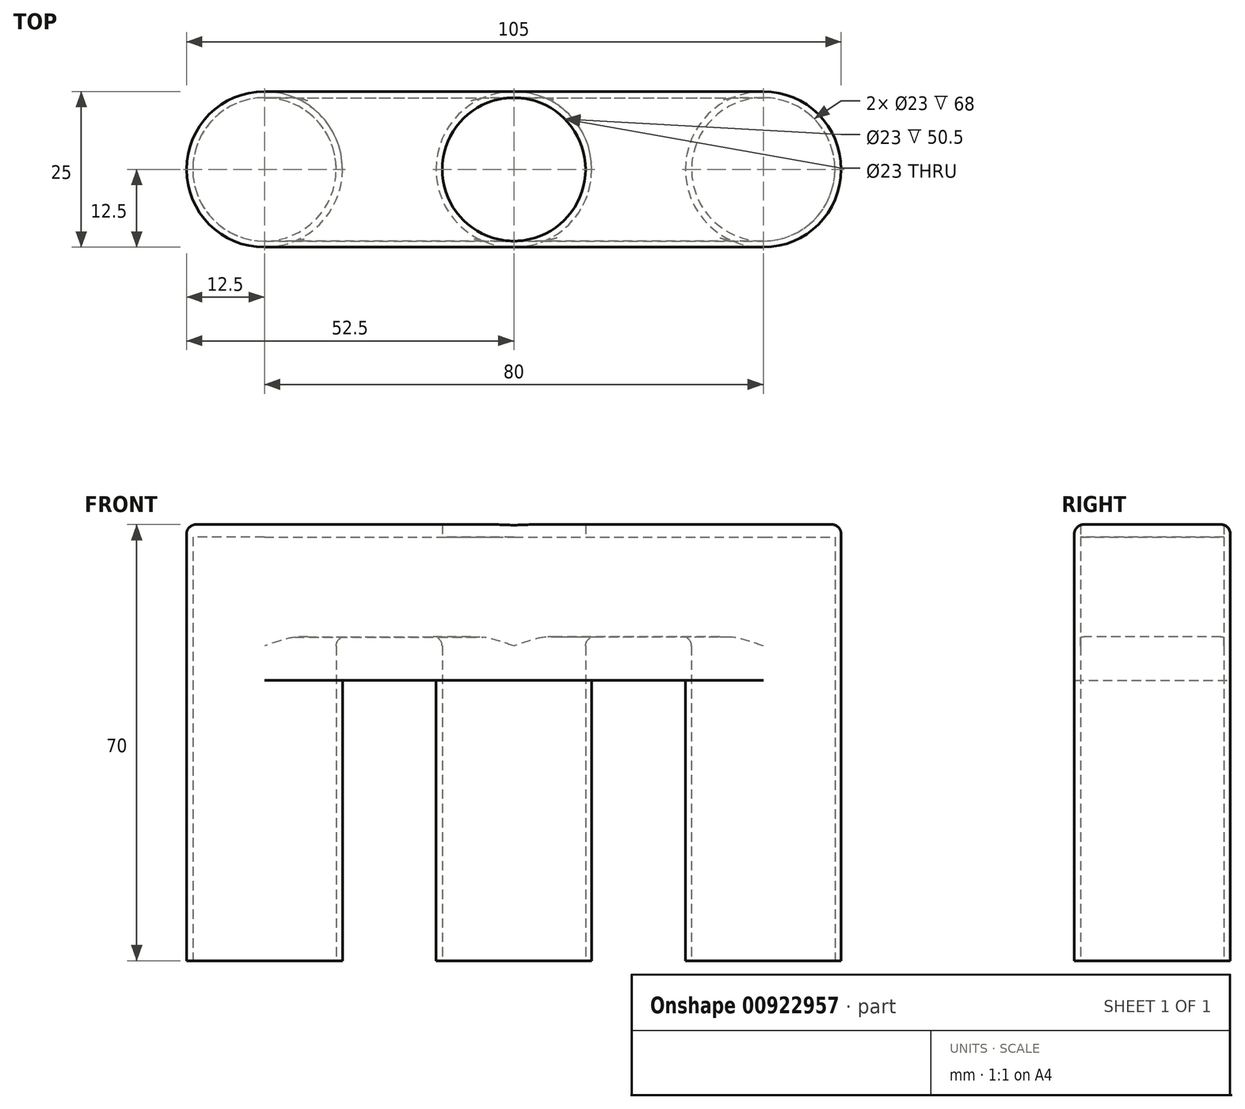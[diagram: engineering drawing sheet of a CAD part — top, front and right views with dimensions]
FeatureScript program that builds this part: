
annotation { "Feature Type Name" : "Feature", "Feature Type Description" : "" }
export const myFeature = defineFeature(function(context is Context, id is Id, definition is map)
    precondition{}
    {
        {
            var Q0;
            Q0=qCreatedBy(makeId("Top.planeOp"),FACE);
            var sketch = newSketch(context, id + "F0", { "sketchPlane" : qUnion([Q0])});
            skCircle(sketch, "E0", {"center": v(0, 0) * mm, "radius": 12.5 * mm});
            skCircle(sketch, "E1", {"center": v(0, 0) * mm, "radius": 11.5 * mm});
            skCircle(sketch, "E2", {"center": v(40, 0) * mm, "radius": 12.5 * mm});
            skCircle(sketch, "E3", {"center": v(40, 0) * mm, "radius": 11.5 * mm});
            skCircle(sketch, "E4", {"center": v(-40, 0) * mm, "radius": 12.5 * mm});
            skCircle(sketch, "E5", {"center": v(-40, 0) * mm, "radius": 11.5 * mm});
            skLineSegment(sketch, "E6", {"start": v(-27.5, 0) * mm, "end": v(-12.5, 0) * mm});
            skLineSegment(sketch, "E7", {"start": v(12.5, 0) * mm, "end": v(27.5, 0) * mm});
            skLineSegment(sketch, "E8", {"start": v(0, 12.5) * mm, "end": v(0, -12.5) * mm, "construction": true});
            skLineSegment(sketch, "E9", {"start": v(-40, 12.5) * mm, "end": v(0, 12.5) * mm});
            skLineSegment(sketch, "E10", {"start": v(0, 12.5) * mm, "end": v(40, 12.5) * mm});
            skLineSegment(sketch, "E11", {"start": v(0, -12.5) * mm, "end": v(40, -12.5) * mm});
            skLineSegment(sketch, "E12", {"start": v(0, -12.5) * mm, "end": v(-40, -12.5) * mm});
            skLineSegment(sketch, "E13", {"start": v(0, 0) * mm, "end": v(52.5, 0) * mm, "construction": true});
            skLineSegment(sketch, "E14", {"start": v(0, 0) * mm, "end": v(-52.5, 0) * mm, "construction": true});
            skLineSegment(sketch, "E15", {"start": v(40, -12.5) * mm, "end": v(40, 12.5) * mm, "construction": true});
            skLineSegment(sketch, "E16", {"start": v(-40, 12.5) * mm, "end": v(-38.5, 12.5) * mm});
            skLineSegment(sketch, "E17", {"start": v(-40, -12.5) * mm, "end": v(-38.5, -12.5) * mm});
            skLineSegment(sketch, "E18", {"start": v(38.5, -12.5) * mm, "end": v(40, -12.5) * mm});
            skLineSegment(sketch, "E19", {"start": v(38.5, 12.5) * mm, "end": v(40, 12.5) * mm});
            skLineSegment(sketch, "E20", {"start": v(-40, 12.5) * mm, "end": v(-40, -12.5) * mm, "construction": true});
            skLineSegment(sketch, "E21", {"start": v(-38.5, 12.5) * mm, "end": v(-40, 0) * mm, "construction": true});
            skLineSegment(sketch, "E22", {"start": v(-38.5, -12.5) * mm, "end": v(-40, 0) * mm, "construction": true});
            skLineSegment(sketch, "E23", {"start": v(38.5, 12.5) * mm, "end": v(40, 0) * mm, "construction": true});
            skLineSegment(sketch, "E24", {"start": v(38.5, -12.5) * mm, "end": v(40, 0) * mm, "construction": true});
            skPoint(sketch, "E25", {"position": v(-40, 11.5) * mm});
            skPoint(sketch, "E26", {"position": v(-40, -11.5) * mm});
            skPoint(sketch, "E27", {"position": v(0, -11.5) * mm});
            skPoint(sketch, "E28", {"position": v(0, 11.5) * mm});
            skPoint(sketch, "E29", {"position": v(40, 11.5) * mm});
            skPoint(sketch, "E30", {"position": v(40, -11.5) * mm});
            skLineSegment(sketch, "E31", {"start": v(-40, 11.5) * mm, "end": v(0, 11.5) * mm});
            skLineSegment(sketch, "E32", {"start": v(40, 11.5) * mm, "end": v(0, 11.5) * mm});
            skLineSegment(sketch, "E33", {"start": v(40, -11.5) * mm, "end": v(0, -11.5) * mm});
            skLineSegment(sketch, "E34", {"start": v(-40, -11.5) * mm, "end": v(0, -11.5) * mm});
            skSolve(sketch);
        }
        {
            var Q0;
            {var subQ0=sQuery(id+"F0.wireOp",EDGE,"05599ef7-5be2-4de1-ad22-cab54b63976f0.MirrorCS");var subQ1=sQuery(id+"F0.wireOp",EDGE,"E4");var subQ2=makeQuery(id+"F0.imprint","INTERSECT",VERTEX,{"disambiguationData":[OD(0.0)],"derivedFrom":[subQ1,subQ0]});Q0=makeQuery(id+"F0.imprint","IMPRINT",FACE,{"disambiguationData":[TD([[makeQuery(id+"F0.imprint","IMPRINT",EDGE,{"disambiguationData":[TD([[subQ2,1.0]])],"derivedFrom":subQ0}),-1.0]])]});}
            var Q1;
            {var subQ1=sQuery(id+"F0.wireOp",EDGE,"E4");var subQ3=sQuery(id+"F0.wireOp",EDGE,"E21");var subQ4=makeQuery(id+"F0.imprint","INTERSECT",VERTEX,{"derivedFrom":[subQ1,subQ3]});Q1=makeQuery(id+"F0.imprint","IMPRINT",FACE,{"disambiguationData":[TD([[makeQuery(id+"F0.imprint","IMPRINT",EDGE,{"disambiguationData":[TD([[subQ4,-1.0]])],"derivedFrom":subQ3}),-1.0]])]});}
            var Q2;
            {var subQ1=sQuery(id+"F0.wireOp",EDGE,"E5");var subQ3=sQuery(id+"F0.wireOp",EDGE,"E21");var subQ4=makeQuery(id+"F0.imprint","INTERSECT",VERTEX,{"derivedFrom":[subQ1,subQ3]});Q2=makeQuery(id+"F0.imprint","IMPRINT",FACE,{"disambiguationData":[TD([[makeQuery(id+"F0.imprint","IMPRINT",EDGE,{"disambiguationData":[TD([[subQ4,1.0]])],"derivedFrom":subQ3}),-1.0]])]});}
            var Q3;
            {var subQ1=sQuery(id+"F0.wireOp",EDGE,"E4");var subQ7=sQuery(id+"F0.wireOp",EDGE,"E31");var subQ9=makeQuery(id+"F0.imprint","INTERSECT",VERTEX,{"derivedFrom":[subQ1,subQ7]});Q3=makeQuery(id+"F0.imprint","IMPRINT",FACE,{"disambiguationData":[TD([[makeQuery(id+"F0.imprint","IMPRINT",EDGE,{"disambiguationData":[TD([[subQ9,1.0]])],"derivedFrom":subQ1}),1.0]])]});}
            var Q4;
            {var subQ0=sQuery(id+"F0.wireOp",EDGE,"E31");var subQ1=sQuery(id+"F0.wireOp",EDGE,"E4");var subQ2=makeQuery(id+"F0.imprint","INTERSECT",VERTEX,{"derivedFrom":[subQ1,subQ0]});Q4=makeQuery(id+"F0.imprint","IMPRINT",FACE,{"disambiguationData":[TD([[makeQuery(id+"F0.imprint","IMPRINT",EDGE,{"disambiguationData":[TD([[subQ2,-1.0]])],"derivedFrom":subQ1}),1.0]])]});}
            var Q5;
            {var subQ5=sQuery(id+"F0.wireOp",EDGE,"05599ef7-5be2-4de1-ad22-cab54b63976f0.MirrorCS");var subQ6=sQuery(id+"F0.wireOp",EDGE,"E4");var subQ7=makeQuery(id+"F0.imprint","INTERSECT",VERTEX,{"disambiguationData":[OD(1.0)],"derivedFrom":[subQ6,subQ5]});Q5=makeQuery(id+"F0.imprint","IMPRINT",FACE,{"disambiguationData":[TD([[makeQuery(id+"F0.imprint","IMPRINT",EDGE,{"disambiguationData":[TD([[subQ7,1.0]])],"derivedFrom":subQ6}),1.0]])]});}
            var Q6;
            {var subQ0=sQuery(id+"F0.wireOp",EDGE,"05599ef7-5be2-4de1-ad22-cab54b63976f0.MirrorCS");var subQ1=sQuery(id+"F0.wireOp",EDGE,"E4");var subQ2=makeQuery(id+"F0.imprint","INTERSECT",VERTEX,{"disambiguationData":[OD(0.0)],"derivedFrom":[subQ1,subQ0]});Q6=makeQuery(id+"F0.imprint","IMPRINT",FACE,{"disambiguationData":[TD([[makeQuery(id+"F0.imprint","IMPRINT",EDGE,{"disambiguationData":[TD([[subQ2,1.0]])],"derivedFrom":subQ0}),1.0]])]});}
            var Q7;
            {var subQ1=sQuery(id+"F0.wireOp",EDGE,"E4");var subQ3=sQuery(id+"F0.wireOp",EDGE,"E22");var subQ4=makeQuery(id+"F0.imprint","INTERSECT",VERTEX,{"derivedFrom":[subQ1,subQ3]});Q7=makeQuery(id+"F0.imprint","IMPRINT",FACE,{"disambiguationData":[TD([[makeQuery(id+"F0.imprint","IMPRINT",EDGE,{"disambiguationData":[TD([[subQ4,-1.0]])],"derivedFrom":subQ3}),1.0]])]});}
            var Q8;
            {var subQ0=sQuery(id+"F0.wireOp",EDGE,"E22");var subQ1=sQuery(id+"F0.wireOp",EDGE,"E4");var subQ2=makeQuery(id+"F0.imprint","INTERSECT",VERTEX,{"derivedFrom":[subQ1,subQ0]});Q8=makeQuery(id+"F0.imprint","IMPRINT",FACE,{"disambiguationData":[TD([[makeQuery(id+"F0.imprint","IMPRINT",EDGE,{"disambiguationData":[TD([[subQ2,-1.0]])],"derivedFrom":subQ1}),1.0]])]});}
            var Q9;
            {var subQ1=sQuery(id+"F0.wireOp",EDGE,"E5");var subQ3=sQuery(id+"F0.wireOp",EDGE,"E22");var subQ4=makeQuery(id+"F0.imprint","INTERSECT",VERTEX,{"derivedFrom":[subQ1,subQ3]});Q9=makeQuery(id+"F0.imprint","IMPRINT",FACE,{"disambiguationData":[TD([[makeQuery(id+"F0.imprint","IMPRINT",EDGE,{"disambiguationData":[TD([[subQ4,1.0]])],"derivedFrom":subQ3}),1.0]])]});}
            var Q10;
            {var subQ1=sQuery(id+"F0.wireOp",EDGE,"E2");var subQ3=sQuery(id+"F0.wireOp",EDGE,"E24");var subQ4=makeQuery(id+"F0.imprint","INTERSECT",VERTEX,{"derivedFrom":[subQ1,subQ3]});Q10=makeQuery(id+"F0.imprint","IMPRINT",FACE,{"disambiguationData":[TD([[makeQuery(id+"F0.imprint","IMPRINT",EDGE,{"disambiguationData":[TD([[subQ4,-1.0]])],"derivedFrom":subQ3}),-1.0]])]});}
            var Q11;
            {var subQ0=sQuery(id+"F0.wireOp",EDGE,"E33");var subQ1=sQuery(id+"F0.wireOp",EDGE,"E2");var subQ2=makeQuery(id+"F0.imprint","INTERSECT",VERTEX,{"derivedFrom":[subQ1,subQ0]});Q11=makeQuery(id+"F0.imprint","IMPRINT",FACE,{"disambiguationData":[TD([[makeQuery(id+"F0.imprint","IMPRINT",EDGE,{"disambiguationData":[TD([[subQ2,-1.0]])],"derivedFrom":subQ1}),1.0]])]});}
            var Q12;
            {var subQ5=sQuery(id+"F0.wireOp",EDGE,"E2");var subQ7=sQuery(id+"F0.wireOp",EDGE,"E13");var subQ9=makeQuery(id+"F0.imprint","INTERSECT",VERTEX,{"disambiguationData":[OD(1.0)],"derivedFrom":[subQ5,subQ7]});Q12=makeQuery(id+"F0.imprint","IMPRINT",FACE,{"disambiguationData":[TD([[makeQuery(id+"F0.imprint","IMPRINT",EDGE,{"disambiguationData":[TD([[subQ9,-1.0]])],"derivedFrom":subQ5}),1.0]])]});}
            var Q13;
            {var subQ1=sQuery(id+"F0.wireOp",EDGE,"E3");var subQ3=sQuery(id+"F0.wireOp",EDGE,"E24");var subQ4=makeQuery(id+"F0.imprint","INTERSECT",VERTEX,{"derivedFrom":[subQ1,subQ3]});Q13=makeQuery(id+"F0.imprint","IMPRINT",FACE,{"disambiguationData":[TD([[makeQuery(id+"F0.imprint","IMPRINT",EDGE,{"disambiguationData":[TD([[subQ4,1.0]])],"derivedFrom":subQ3}),-1.0]])]});}
            var Q14;
            {var subQ0=sQuery(id+"F0.wireOp",EDGE,"E13");var subQ1=sQuery(id+"F0.wireOp",EDGE,"E2");var subQ2=makeQuery(id+"F0.imprint","INTERSECT",VERTEX,{"disambiguationData":[OD(0.0)],"derivedFrom":[subQ1,subQ0]});Q14=makeQuery(id+"F0.imprint","IMPRINT",FACE,{"disambiguationData":[TD([[makeQuery(id+"F0.imprint","IMPRINT",EDGE,{"disambiguationData":[TD([[subQ2,1.0]])],"derivedFrom":subQ0}),-1.0]])]});}
            var Q15;
            {var subQ0=sQuery(id+"F0.wireOp",EDGE,"E13");var subQ1=sQuery(id+"F0.wireOp",EDGE,"E2");var subQ2=makeQuery(id+"F0.imprint","INTERSECT",VERTEX,{"disambiguationData":[OD(0.0)],"derivedFrom":[subQ1,subQ0]});Q15=makeQuery(id+"F0.imprint","IMPRINT",FACE,{"disambiguationData":[TD([[makeQuery(id+"F0.imprint","IMPRINT",EDGE,{"disambiguationData":[TD([[subQ2,1.0]])],"derivedFrom":subQ0}),1.0]])]});}
            var Q16;
            {var subQ3=sQuery(id+"F0.wireOp",EDGE,"E32");var subQ6=sQuery(id+"F0.wireOp",EDGE,"E2");var subQ9=makeQuery(id+"F0.imprint","INTERSECT",VERTEX,{"derivedFrom":[subQ6,subQ3]});Q16=makeQuery(id+"F0.imprint","IMPRINT",FACE,{"disambiguationData":[TD([[makeQuery(id+"F0.imprint","IMPRINT",EDGE,{"disambiguationData":[TD([[subQ9,-1.0]])],"derivedFrom":subQ6}),1.0]])]});}
            var Q17;
            {var subQ0=sQuery(id+"F0.wireOp",EDGE,"E23");var subQ1=sQuery(id+"F0.wireOp",EDGE,"E2");var subQ2=makeQuery(id+"F0.imprint","INTERSECT",VERTEX,{"derivedFrom":[subQ1,subQ0]});Q17=makeQuery(id+"F0.imprint","IMPRINT",FACE,{"disambiguationData":[TD([[makeQuery(id+"F0.imprint","IMPRINT",EDGE,{"disambiguationData":[TD([[subQ2,-1.0]])],"derivedFrom":subQ1}),1.0]])]});}
            var Q18;
            {var subQ1=sQuery(id+"F0.wireOp",EDGE,"E2");var subQ3=sQuery(id+"F0.wireOp",EDGE,"E23");var subQ4=makeQuery(id+"F0.imprint","INTERSECT",VERTEX,{"derivedFrom":[subQ1,subQ3]});Q18=makeQuery(id+"F0.imprint","IMPRINT",FACE,{"disambiguationData":[TD([[makeQuery(id+"F0.imprint","IMPRINT",EDGE,{"disambiguationData":[TD([[subQ4,-1.0]])],"derivedFrom":subQ3}),1.0]])]});}
            var Q19;
            {var subQ1=sQuery(id+"F0.wireOp",EDGE,"E3");var subQ3=sQuery(id+"F0.wireOp",EDGE,"E23");var subQ4=makeQuery(id+"F0.imprint","INTERSECT",VERTEX,{"derivedFrom":[subQ1,subQ3]});Q19=makeQuery(id+"F0.imprint","IMPRINT",FACE,{"disambiguationData":[TD([[makeQuery(id+"F0.imprint","IMPRINT",EDGE,{"disambiguationData":[TD([[subQ4,1.0]])],"derivedFrom":subQ3}),1.0]])]});}
            var Q20;
            {var subQ0=sQuery(id+"F0.wireOp",EDGE,"E13");var subQ1=sQuery(id+"F0.wireOp",EDGE,"E0");var subQ2=makeQuery(id+"F0.imprint","INTERSECT",VERTEX,{"derivedFrom":[subQ1,subQ0]});Q20=makeQuery(id+"F0.imprint","IMPRINT",FACE,{"disambiguationData":[TD([[makeQuery(id+"F0.imprint","IMPRINT",EDGE,{"disambiguationData":[TD([[subQ2,1.0]])],"derivedFrom":subQ1}),1.0]])]});}
            var Q21;
            {var subQ1=sQuery(id+"F0.wireOp",EDGE,"E0");var subQ3=sQuery(id+"F0.wireOp",EDGE,"E33");var subQ4=makeQuery(id+"F0.imprint","INTERSECT",VERTEX,{"derivedFrom":[subQ1,subQ3]});Q21=makeQuery(id+"F0.imprint","IMPRINT",FACE,{"disambiguationData":[TD([[makeQuery(id+"F0.imprint","IMPRINT",EDGE,{"disambiguationData":[TD([[subQ4,1.0]])],"derivedFrom":subQ1}),1.0]])]});}
            var Q22;
            {var subQ1=sQuery(id+"F0.wireOp",EDGE,"E0");var subQ3=sQuery(id+"F0.wireOp",EDGE,"E34");var subQ4=makeQuery(id+"F0.imprint","INTERSECT",VERTEX,{"derivedFrom":[subQ1,subQ3]});Q22=makeQuery(id+"F0.imprint","IMPRINT",FACE,{"disambiguationData":[TD([[makeQuery(id+"F0.imprint","IMPRINT",EDGE,{"disambiguationData":[TD([[subQ4,-1.0]])],"derivedFrom":subQ1}),1.0]])]});}
            var Q23;
            {var subQ0=sQuery(id+"F0.wireOp",EDGE,"05599ef7-5be2-4de1-ad22-cab54b63976f0.MirrorCS");var subQ1=sQuery(id+"F0.wireOp",EDGE,"E0");var subQ2=makeQuery(id+"F0.imprint","INTERSECT",VERTEX,{"derivedFrom":[subQ1,subQ0]});Q23=makeQuery(id+"F0.imprint","IMPRINT",FACE,{"disambiguationData":[TD([[makeQuery(id+"F0.imprint","IMPRINT",EDGE,{"disambiguationData":[TD([[subQ2,-1.0]])],"derivedFrom":subQ1}),1.0]])]});}
            var Q24;
            {var subQ0=sQuery(id+"F0.wireOp",EDGE,"E31");var subQ1=sQuery(id+"F0.wireOp",EDGE,"E0");var subQ2=makeQuery(id+"F0.imprint","INTERSECT",VERTEX,{"derivedFrom":[subQ1,subQ0]});Q24=makeQuery(id+"F0.imprint","IMPRINT",FACE,{"disambiguationData":[TD([[makeQuery(id+"F0.imprint","IMPRINT",EDGE,{"disambiguationData":[TD([[subQ2,-1.0]])],"derivedFrom":subQ1}),1.0]])]});}
            var Q25;
            {var subQ0=sQuery(id+"F0.wireOp",EDGE,"E32");var subQ1=sQuery(id+"F0.wireOp",EDGE,"E0");var subQ2=makeQuery(id+"F0.imprint","INTERSECT",VERTEX,{"derivedFrom":[subQ1,subQ0]});Q25=makeQuery(id+"F0.imprint","IMPRINT",FACE,{"disambiguationData":[TD([[makeQuery(id+"F0.imprint","IMPRINT",EDGE,{"disambiguationData":[TD([[subQ2,1.0]])],"derivedFrom":subQ1}),1.0]])]});}
            var Q26;
            {var subQ1=sQuery(id+"F0.wireOp",EDGE,"E0");var subQ3=sQuery(id+"F0.wireOp",EDGE,"E32");var subQ4=makeQuery(id+"F0.imprint","INTERSECT",VERTEX,{"derivedFrom":[subQ1,subQ3]});Q26=makeQuery(id+"F0.imprint","IMPRINT",FACE,{"disambiguationData":[TD([[makeQuery(id+"F0.imprint","IMPRINT",EDGE,{"disambiguationData":[TD([[subQ4,-1.0]])],"derivedFrom":subQ1}),1.0]])]});}
            var Q27;
            {var subQ1=sQuery(id+"F0.wireOp",EDGE,"E0");var subQ3=sQuery(id+"F0.wireOp",EDGE,"E31");var subQ4=makeQuery(id+"F0.imprint","INTERSECT",VERTEX,{"derivedFrom":[subQ1,subQ3]});Q27=makeQuery(id+"F0.imprint","IMPRINT",FACE,{"disambiguationData":[TD([[makeQuery(id+"F0.imprint","IMPRINT",EDGE,{"disambiguationData":[TD([[subQ4,1.0]])],"derivedFrom":subQ1}),1.0]])]});}
            var Q28;
            {var subQ0=sQuery(id+"F0.wireOp",EDGE,"E14");var subQ1=sQuery(id+"F0.wireOp",EDGE,"E4");var subQ2=makeQuery(id+"F0.imprint","INTERSECT",VERTEX,{"disambiguationData":[OD(0.0)],"derivedFrom":[subQ1,subQ0]});Q28=makeQuery(id+"F0.imprint","IMPRINT",FACE,{"disambiguationData":[TD([[makeQuery(id+"F0.imprint","IMPRINT",EDGE,{"disambiguationData":[TD([[subQ2,1.0]])],"derivedFrom":subQ0}),-1.0]])]});}
            var Q29;
            {var subQ0=sQuery(id+"F0.wireOp",EDGE,"E14");var subQ1=sQuery(id+"F0.wireOp",EDGE,"E4");var subQ2=makeQuery(id+"F0.imprint","INTERSECT",VERTEX,{"disambiguationData":[OD(0.0)],"derivedFrom":[subQ1,subQ0]});Q29=makeQuery(id+"F0.imprint","IMPRINT",FACE,{"disambiguationData":[TD([[makeQuery(id+"F0.imprint","IMPRINT",EDGE,{"disambiguationData":[TD([[subQ2,1.0]])],"derivedFrom":subQ0}),1.0]])]});}
            var Q30;
            {var subQ0=sQuery(id+"F0.wireOp",EDGE,"E14");var subQ1=sQuery(id+"F0.wireOp",EDGE,"E0");var subQ2=makeQuery(id+"F0.imprint","INTERSECT",VERTEX,{"derivedFrom":[subQ1,subQ0]});Q30=makeQuery(id+"F0.imprint","IMPRINT",FACE,{"disambiguationData":[TD([[makeQuery(id+"F0.imprint","IMPRINT",EDGE,{"disambiguationData":[TD([[subQ2,-1.0]])],"derivedFrom":subQ1}),1.0]])]});}
            extrude(context, id + "F1", {"entities" : qUnion([Q0, Q1, Q2, Q3, Q4, Q5, Q6, Q7, Q8, Q9, Q10, Q11, Q12, Q13, Q14, Q15, Q16, Q17, Q18, Q19, Q20, Q21, Q22, Q23, Q24, Q25, Q26, Q27, Q28, Q29, Q30]), "depth" : 50 * mm, "offsetDistance" : 25 * mm});
        }
        {
            var Q0;
            {var subQ0=sQuery(id+"F0.wireOp",EDGE,"E6");Q0=makeQuery(id+"F0.imprint","IMPRINT",FACE,{"disambiguationData":[TD([[makeQuery(id+"F0.imprint","IMPRINT",EDGE,{"derivedFrom":subQ0}),1.0]])]});}
            var Q1;
            {var subQ0=sQuery(id+"F0.wireOp",EDGE,"E6");Q1=makeQuery(id+"F0.imprint","IMPRINT",FACE,{"disambiguationData":[TD([[makeQuery(id+"F0.imprint","IMPRINT",EDGE,{"derivedFrom":subQ0}),-1.0]])]});}
            var Q2;
            {var subQ4=sQuery(id+"F0.wireOp",EDGE,"E12");Q2=makeQuery(id+"F0.imprint","IMPRINT",FACE,{"disambiguationData":[TD([[makeQuery(id+"F0.imprint","IMPRINT",EDGE,{"derivedFrom":subQ4}),-1.0]])]});}
            var Q3;
            {var subQ0=sQuery(id+"F0.wireOp",EDGE,"E0");var subQ2=sQuery(id+"F0.wireOp",EDGE,"E34");var subQ3=makeQuery(id+"F0.imprint","INTERSECT",VERTEX,{"derivedFrom":[subQ0,subQ2]});Q3=makeQuery(id+"F0.imprint","IMPRINT",FACE,{"disambiguationData":[TD([[makeQuery(id+"F0.imprint","IMPRINT",EDGE,{"disambiguationData":[TD([[subQ3,-1.0]])],"derivedFrom":subQ0}),1.0]])]});}
            var Q4;
            {var subQ3=sQuery(id+"F0.wireOp",EDGE,"E0");var subQ8=makeQuery(id+"F0.imprint","INTERSECT",VERTEX,{"derivedFrom":[subQ3,sQuery(id+"F0.wireOp",EDGE,"E7")]});Q4=makeQuery(id+"F0.imprint","IMPRINT",FACE,{"disambiguationData":[TD([[makeQuery(id+"F0.imprint","IMPRINT",EDGE,{"disambiguationData":[TD([[subQ8,-1.0]])],"derivedFrom":subQ3}),1.0]])]});}
            var Q5;
            {var subQ3=sQuery(id+"F0.wireOp",EDGE,"E0");var subQ5=makeQuery(id+"F0.imprint","INTERSECT",VERTEX,{"derivedFrom":[subQ3,sQuery(id+"F0.wireOp",EDGE,"E6")]});Q5=makeQuery(id+"F0.imprint","IMPRINT",FACE,{"disambiguationData":[TD([[makeQuery(id+"F0.imprint","IMPRINT",EDGE,{"disambiguationData":[TD([[subQ5,1.0]])],"derivedFrom":subQ3}),1.0]])]});}
            var Q6;
            {var subQ1=sQuery(id+"F0.wireOp",EDGE,"E11");Q6=makeQuery(id+"F0.imprint","IMPRINT",FACE,{"disambiguationData":[TD([[makeQuery(id+"F0.imprint","IMPRINT",EDGE,{"derivedFrom":subQ1}),1.0]])]});}
            var Q7;
            {var subQ0=sQuery(id+"F0.wireOp",EDGE,"E0");var subQ2=sQuery(id+"F0.wireOp",EDGE,"E32");var subQ3=makeQuery(id+"F0.imprint","INTERSECT",VERTEX,{"derivedFrom":[subQ0,subQ2]});Q7=makeQuery(id+"F0.imprint","IMPRINT",FACE,{"disambiguationData":[TD([[makeQuery(id+"F0.imprint","IMPRINT",EDGE,{"disambiguationData":[TD([[subQ3,-1.0]])],"derivedFrom":subQ0}),1.0]])]});}
            var Q8;
            {var subQ1=sQuery(id+"F0.wireOp",EDGE,"E10");Q8=makeQuery(id+"F0.imprint","IMPRINT",FACE,{"disambiguationData":[TD([[makeQuery(id+"F0.imprint","IMPRINT",EDGE,{"derivedFrom":subQ1}),-1.0]])]});}
            var Q9;
            {var subQ1=sQuery(id+"F0.wireOp",EDGE,"E9");Q9=makeQuery(id+"F0.imprint","IMPRINT",FACE,{"disambiguationData":[TD([[makeQuery(id+"F0.imprint","IMPRINT",EDGE,{"derivedFrom":subQ1}),-1.0]])]});}
            var Q10;
            {var subQ0=sQuery(id+"F0.wireOp",EDGE,"E7");Q10=makeQuery(id+"F0.imprint","IMPRINT",FACE,{"disambiguationData":[TD([[makeQuery(id+"F0.imprint","IMPRINT",EDGE,{"derivedFrom":subQ0}),1.0]])]});}
            var Q11;
            {var subQ0=sQuery(id+"F0.wireOp",EDGE,"E7");Q11=makeQuery(id+"F0.imprint","IMPRINT",FACE,{"disambiguationData":[TD([[makeQuery(id+"F0.imprint","IMPRINT",EDGE,{"derivedFrom":subQ0}),-1.0]])]});}
            var Q12;
            {var subQ5=sQuery(id+"F0.wireOp",EDGE,"E2");var subQ7=makeQuery(id+"F0.imprint","INTERSECT",VERTEX,{"derivedFrom":[subQ5,sQuery(id+"F0.wireOp",EDGE,"E7")]});Q12=makeQuery(id+"F0.imprint","IMPRINT",FACE,{"disambiguationData":[TD([[makeQuery(id+"F0.imprint","IMPRINT",EDGE,{"disambiguationData":[TD([[subQ7,1.0]])],"derivedFrom":subQ5}),1.0]])]});}
            var Q13;
            {var subQ5=sQuery(id+"F0.wireOp",EDGE,"E2");var subQ7=makeQuery(id+"F0.imprint","INTERSECT",VERTEX,{"derivedFrom":[subQ5,sQuery(id+"F0.wireOp",EDGE,"E19")]});Q13=makeQuery(id+"F0.imprint","IMPRINT",FACE,{"disambiguationData":[TD([[makeQuery(id+"F0.imprint","IMPRINT",EDGE,{"disambiguationData":[TD([[subQ7,-1.0]])],"derivedFrom":subQ5}),1.0]])]});}
            var Q14;
            {var subQ3=sQuery(id+"F0.wireOp",EDGE,"E4");var subQ7=makeQuery(id+"F0.imprint","INTERSECT",VERTEX,{"derivedFrom":[subQ3,sQuery(id+"F0.wireOp",EDGE,"E6")]});Q14=makeQuery(id+"F0.imprint","IMPRINT",FACE,{"disambiguationData":[TD([[makeQuery(id+"F0.imprint","IMPRINT",EDGE,{"disambiguationData":[TD([[subQ7,-1.0]])],"derivedFrom":subQ3}),1.0]])]});}
            var Q15;
            {var subQ5=sQuery(id+"F0.wireOp",EDGE,"E4");var subQ8=makeQuery(id+"F0.imprint","INTERSECT",VERTEX,{"derivedFrom":[subQ5,sQuery(id+"F0.wireOp",EDGE,"E16")]});Q15=makeQuery(id+"F0.imprint","IMPRINT",FACE,{"disambiguationData":[TD([[makeQuery(id+"F0.imprint","IMPRINT",EDGE,{"disambiguationData":[TD([[subQ8,1.0]])],"derivedFrom":subQ5}),1.0]])]});}
            extrude(context, id + "F2", {"entities" : qUnion([Q0, Q1, Q2, Q3, Q4, Q5, Q6, Q7, Q8, Q9, Q10, Q11, Q12, Q13, Q14, Q15]), "depth" : 52 * mm, "offsetDistance" : 25 * mm, "hasSecondDirection" : true, "secondDirectionOppositeDirection" : false, "secondDirectionDepth" : 45 * mm});
        }
        {
            var Q0;
            {var subQ0=sQuery(id+"F0.wireOp",EDGE,"E3");var subQ1=sQuery(id+"F0.wireOp",EDGE,"E1");var subQ2=makeQuery(id+"F2.opExtrude","CAP_FACE",FACE,{"disambiguationData":[OSD([subQ1,sQuery(id+"F0.wireOp",EDGE,"E2"),subQ0,sQuery(id+"F0.wireOp",EDGE,"E4"),sQuery(id+"F0.wireOp",EDGE,"E5"),sQuery(id+"F0.wireOp",EDGE,"E9"),sQuery(id+"F0.wireOp",EDGE,"E10"),sQuery(id+"F0.wireOp",EDGE,"E11"),sQuery(id+"F0.wireOp",EDGE,"E12"),sQuery(id+"F0.wireOp",EDGE,"E16"),sQuery(id+"F0.wireOp",EDGE,"E17"),sQuery(id+"F0.wireOp",EDGE,"E18"),sQuery(id+"F0.wireOp",EDGE,"E19")])],"isStart":false});Q0=makeQuery(id+"F4.boolean.opBoolean","SPLIT",FACE,{"disambiguationData":[TD([makeQuery(id+"F2.opExtrude","SWEPT_FACE",FACE,{"disambiguationData":[OSD([subQ0])]})])],"derivedFrom":subQ2});}
            var Q1;
            {var subQ0=sQuery(id+"F0.wireOp",EDGE,"E5");var subQ1=sQuery(id+"F0.wireOp",EDGE,"E1");var subQ2=makeQuery(id+"F2.opExtrude","CAP_FACE",FACE,{"disambiguationData":[OSD([subQ1,sQuery(id+"F0.wireOp",EDGE,"E2"),sQuery(id+"F0.wireOp",EDGE,"E3"),sQuery(id+"F0.wireOp",EDGE,"E4"),subQ0,sQuery(id+"F0.wireOp",EDGE,"E9"),sQuery(id+"F0.wireOp",EDGE,"E10"),sQuery(id+"F0.wireOp",EDGE,"E11"),sQuery(id+"F0.wireOp",EDGE,"E12"),sQuery(id+"F0.wireOp",EDGE,"E16"),sQuery(id+"F0.wireOp",EDGE,"E17"),sQuery(id+"F0.wireOp",EDGE,"E18"),sQuery(id+"F0.wireOp",EDGE,"E19")])],"isStart":false});Q1=makeQuery(id+"F4.boolean.opBoolean","SPLIT",FACE,{"disambiguationData":[TD([makeQuery(id+"F2.opExtrude","SWEPT_FACE",FACE,{"disambiguationData":[OSD([subQ0])]})])],"derivedFrom":subQ2});}
            fillet(context, id + "F3", {"entities" : qUnion([Q0, Q1]), "radius" : 1.5 * mm, "tangentPropagation" : true, "allowEdgeOverflow" : false});
        }
        {
            var Q0;
            {var subQ4=sQuery(id+"F0.wireOp",EDGE,"E12");Q0=makeQuery(id+"F0.imprint","IMPRINT",FACE,{"disambiguationData":[TD([[makeQuery(id+"F0.imprint","IMPRINT",EDGE,{"derivedFrom":subQ4}),-1.0]])]});}
            var Q1;
            {var subQ5=sQuery(id+"F0.wireOp",EDGE,"E4");var subQ8=makeQuery(id+"F0.imprint","INTERSECT",VERTEX,{"derivedFrom":[subQ5,sQuery(id+"F0.wireOp",EDGE,"E16")]});Q1=makeQuery(id+"F0.imprint","IMPRINT",FACE,{"disambiguationData":[TD([[makeQuery(id+"F0.imprint","IMPRINT",EDGE,{"disambiguationData":[TD([[subQ8,1.0]])],"derivedFrom":subQ5}),1.0]])]});}
            var Q2;
            {var subQ1=sQuery(id+"F0.wireOp",EDGE,"E9");Q2=makeQuery(id+"F0.imprint","IMPRINT",FACE,{"disambiguationData":[TD([[makeQuery(id+"F0.imprint","IMPRINT",EDGE,{"derivedFrom":subQ1}),-1.0]])]});}
            var Q3;
            {var subQ0=sQuery(id+"F0.wireOp",EDGE,"E0");var subQ2=sQuery(id+"F0.wireOp",EDGE,"E32");var subQ3=makeQuery(id+"F0.imprint","INTERSECT",VERTEX,{"derivedFrom":[subQ0,subQ2]});Q3=makeQuery(id+"F0.imprint","IMPRINT",FACE,{"disambiguationData":[TD([[makeQuery(id+"F0.imprint","IMPRINT",EDGE,{"disambiguationData":[TD([[subQ3,-1.0]])],"derivedFrom":subQ0}),1.0]])]});}
            var Q4;
            {var subQ1=sQuery(id+"F0.wireOp",EDGE,"E10");Q4=makeQuery(id+"F0.imprint","IMPRINT",FACE,{"disambiguationData":[TD([[makeQuery(id+"F0.imprint","IMPRINT",EDGE,{"derivedFrom":subQ1}),-1.0]])]});}
            var Q5;
            {var subQ5=sQuery(id+"F0.wireOp",EDGE,"E2");var subQ7=makeQuery(id+"F0.imprint","INTERSECT",VERTEX,{"derivedFrom":[subQ5,sQuery(id+"F0.wireOp",EDGE,"E19")]});Q5=makeQuery(id+"F0.imprint","IMPRINT",FACE,{"disambiguationData":[TD([[makeQuery(id+"F0.imprint","IMPRINT",EDGE,{"disambiguationData":[TD([[subQ7,-1.0]])],"derivedFrom":subQ5}),1.0]])]});}
            var Q6;
            {var subQ1=sQuery(id+"F0.wireOp",EDGE,"E11");Q6=makeQuery(id+"F0.imprint","IMPRINT",FACE,{"disambiguationData":[TD([[makeQuery(id+"F0.imprint","IMPRINT",EDGE,{"derivedFrom":subQ1}),1.0]])]});}
            var Q7;
            {var subQ0=sQuery(id+"F0.wireOp",EDGE,"E0");var subQ2=sQuery(id+"F0.wireOp",EDGE,"E34");var subQ3=makeQuery(id+"F0.imprint","INTERSECT",VERTEX,{"derivedFrom":[subQ0,subQ2]});Q7=makeQuery(id+"F0.imprint","IMPRINT",FACE,{"disambiguationData":[TD([[makeQuery(id+"F0.imprint","IMPRINT",EDGE,{"disambiguationData":[TD([[subQ3,-1.0]])],"derivedFrom":subQ0}),1.0]])]});}
            extrude(context, id + "F4", {"entities" : qUnion([Q0, Q1, Q2, Q3, Q4, Q5, Q6, Q7]), "operationType" : NewBodyOperationType.ADD, "depth" : 68 * mm, "offsetDistance" : 25 * mm, "hasSecondDirection" : true, "secondDirectionOppositeDirection" : false, "secondDirectionDepth" : 50 * mm});
        }
        {
            var Q0;
            {var subQ4=sQuery(id+"F0.wireOp",EDGE,"E12");Q0=makeQuery(id+"F0.imprint","IMPRINT",FACE,{"disambiguationData":[TD([[makeQuery(id+"F0.imprint","IMPRINT",EDGE,{"derivedFrom":subQ4}),-1.0]])]});}
            var Q1;
            {var subQ0=sQuery(id+"F0.wireOp",EDGE,"E6");Q1=makeQuery(id+"F0.imprint","IMPRINT",FACE,{"disambiguationData":[TD([[makeQuery(id+"F0.imprint","IMPRINT",EDGE,{"derivedFrom":subQ0}),-1.0]])]});}
            var Q2;
            {var subQ0=sQuery(id+"F0.wireOp",EDGE,"E6");Q2=makeQuery(id+"F0.imprint","IMPRINT",FACE,{"disambiguationData":[TD([[makeQuery(id+"F0.imprint","IMPRINT",EDGE,{"derivedFrom":subQ0}),1.0]])]});}
            var Q3;
            {var subQ3=sQuery(id+"F0.wireOp",EDGE,"E4");var subQ7=makeQuery(id+"F0.imprint","INTERSECT",VERTEX,{"derivedFrom":[subQ3,sQuery(id+"F0.wireOp",EDGE,"E6")]});Q3=makeQuery(id+"F0.imprint","IMPRINT",FACE,{"disambiguationData":[TD([[makeQuery(id+"F0.imprint","IMPRINT",EDGE,{"disambiguationData":[TD([[subQ7,-1.0]])],"derivedFrom":subQ3}),1.0]])]});}
            var Q4;
            {var subQ0=sQuery(id+"F0.wireOp",EDGE,"E5");var subQ1=makeQuery(id+"F0.imprint","INTERSECT",VERTEX,{"derivedFrom":[subQ0,sQuery(id+"F0.wireOp",EDGE,"E31")]});Q4=makeQuery(id+"F0.imprint","IMPRINT",FACE,{"disambiguationData":[TD([[makeQuery(id+"F0.imprint","IMPRINT",EDGE,{"disambiguationData":[TD([[subQ1,-1.0]])],"derivedFrom":subQ0}),1.0]])]});}
            var Q5;
            {var subQ5=sQuery(id+"F0.wireOp",EDGE,"E4");var subQ8=makeQuery(id+"F0.imprint","INTERSECT",VERTEX,{"derivedFrom":[subQ5,sQuery(id+"F0.wireOp",EDGE,"E16")]});Q5=makeQuery(id+"F0.imprint","IMPRINT",FACE,{"disambiguationData":[TD([[makeQuery(id+"F0.imprint","IMPRINT",EDGE,{"disambiguationData":[TD([[subQ8,1.0]])],"derivedFrom":subQ5}),1.0]])]});}
            var Q6;
            {var subQ1=sQuery(id+"F0.wireOp",EDGE,"E9");Q6=makeQuery(id+"F0.imprint","IMPRINT",FACE,{"disambiguationData":[TD([[makeQuery(id+"F0.imprint","IMPRINT",EDGE,{"derivedFrom":subQ1}),-1.0]])]});}
            var Q7;
            {var subQ3=sQuery(id+"F0.wireOp",EDGE,"E0");var subQ5=makeQuery(id+"F0.imprint","INTERSECT",VERTEX,{"derivedFrom":[subQ3,sQuery(id+"F0.wireOp",EDGE,"E6")]});Q7=makeQuery(id+"F0.imprint","IMPRINT",FACE,{"disambiguationData":[TD([[makeQuery(id+"F0.imprint","IMPRINT",EDGE,{"disambiguationData":[TD([[subQ5,1.0]])],"derivedFrom":subQ3}),1.0]])]});}
            var Q8;
            {var subQ3=sQuery(id+"F0.wireOp",EDGE,"E0");var subQ8=makeQuery(id+"F0.imprint","INTERSECT",VERTEX,{"derivedFrom":[subQ3,sQuery(id+"F0.wireOp",EDGE,"E7")]});Q8=makeQuery(id+"F0.imprint","IMPRINT",FACE,{"disambiguationData":[TD([[makeQuery(id+"F0.imprint","IMPRINT",EDGE,{"disambiguationData":[TD([[subQ8,-1.0]])],"derivedFrom":subQ3}),1.0]])]});}
            var Q9;
            {var subQ0=sQuery(id+"F0.wireOp",EDGE,"E0");var subQ2=sQuery(id+"F0.wireOp",EDGE,"E34");var subQ3=makeQuery(id+"F0.imprint","INTERSECT",VERTEX,{"derivedFrom":[subQ0,subQ2]});Q9=makeQuery(id+"F0.imprint","IMPRINT",FACE,{"disambiguationData":[TD([[makeQuery(id+"F0.imprint","IMPRINT",EDGE,{"disambiguationData":[TD([[subQ3,-1.0]])],"derivedFrom":subQ0}),1.0]])]});}
            var Q10;
            {var subQ1=sQuery(id+"F0.wireOp",EDGE,"E11");Q10=makeQuery(id+"F0.imprint","IMPRINT",FACE,{"disambiguationData":[TD([[makeQuery(id+"F0.imprint","IMPRINT",EDGE,{"derivedFrom":subQ1}),1.0]])]});}
            var Q11;
            {var subQ0=sQuery(id+"F0.wireOp",EDGE,"E7");Q11=makeQuery(id+"F0.imprint","IMPRINT",FACE,{"disambiguationData":[TD([[makeQuery(id+"F0.imprint","IMPRINT",EDGE,{"derivedFrom":subQ0}),-1.0]])]});}
            var Q12;
            {var subQ0=sQuery(id+"F0.wireOp",EDGE,"E7");Q12=makeQuery(id+"F0.imprint","IMPRINT",FACE,{"disambiguationData":[TD([[makeQuery(id+"F0.imprint","IMPRINT",EDGE,{"derivedFrom":subQ0}),1.0]])]});}
            var Q13;
            {var subQ5=sQuery(id+"F0.wireOp",EDGE,"E2");var subQ7=makeQuery(id+"F0.imprint","INTERSECT",VERTEX,{"derivedFrom":[subQ5,sQuery(id+"F0.wireOp",EDGE,"E7")]});Q13=makeQuery(id+"F0.imprint","IMPRINT",FACE,{"disambiguationData":[TD([[makeQuery(id+"F0.imprint","IMPRINT",EDGE,{"disambiguationData":[TD([[subQ7,1.0]])],"derivedFrom":subQ5}),1.0]])]});}
            var Q14;
            {var subQ0=sQuery(id+"F0.wireOp",EDGE,"E3");var subQ1=makeQuery(id+"F0.imprint","INTERSECT",VERTEX,{"derivedFrom":[subQ0,sQuery(id+"F0.wireOp",EDGE,"E32")]});Q14=makeQuery(id+"F0.imprint","IMPRINT",FACE,{"disambiguationData":[TD([[makeQuery(id+"F0.imprint","IMPRINT",EDGE,{"disambiguationData":[TD([[subQ1,-1.0]])],"derivedFrom":subQ0}),1.0]])]});}
            var Q15;
            {var subQ1=sQuery(id+"F0.wireOp",EDGE,"E10");Q15=makeQuery(id+"F0.imprint","IMPRINT",FACE,{"disambiguationData":[TD([[makeQuery(id+"F0.imprint","IMPRINT",EDGE,{"derivedFrom":subQ1}),-1.0]])]});}
            var Q16;
            {var subQ0=sQuery(id+"F0.wireOp",EDGE,"E0");var subQ2=sQuery(id+"F0.wireOp",EDGE,"E32");var subQ3=makeQuery(id+"F0.imprint","INTERSECT",VERTEX,{"derivedFrom":[subQ0,subQ2]});Q16=makeQuery(id+"F0.imprint","IMPRINT",FACE,{"disambiguationData":[TD([[makeQuery(id+"F0.imprint","IMPRINT",EDGE,{"disambiguationData":[TD([[subQ3,-1.0]])],"derivedFrom":subQ0}),1.0]])]});}
            var Q17;
            {var subQ5=sQuery(id+"F0.wireOp",EDGE,"E2");var subQ7=makeQuery(id+"F0.imprint","INTERSECT",VERTEX,{"derivedFrom":[subQ5,sQuery(id+"F0.wireOp",EDGE,"E19")]});Q17=makeQuery(id+"F0.imprint","IMPRINT",FACE,{"disambiguationData":[TD([[makeQuery(id+"F0.imprint","IMPRINT",EDGE,{"disambiguationData":[TD([[subQ7,-1.0]])],"derivedFrom":subQ5}),1.0]])]});}
            extrude(context, id + "F5", {"entities" : qUnion([Q0, Q1, Q2, Q3, Q4, Q5, Q6, Q7, Q8, Q9, Q10, Q11, Q12, Q13, Q14, Q15, Q16, Q17]), "operationType" : NewBodyOperationType.ADD, "depth" : 70 * mm, "offsetDistance" : 25 * mm, "hasSecondDirection" : true, "secondDirectionOppositeDirection" : false, "secondDirectionDepth" : 68 * mm});
        }
        {
            var Q0;
            Q0=makeQuery(id+"F5.opExtrude","CAP_EDGE",EDGE,{"disambiguationData":[OSD([sQuery(id+"F0.wireOp",EDGE,"E4")])],"isStart":false});
            fillet(context, id + "F6", {"entities" : qUnion([Q0]), "radius" : 1.5 * mm, "tangentPropagation" : true, "allowEdgeOverflow" : false});
        }
    });
